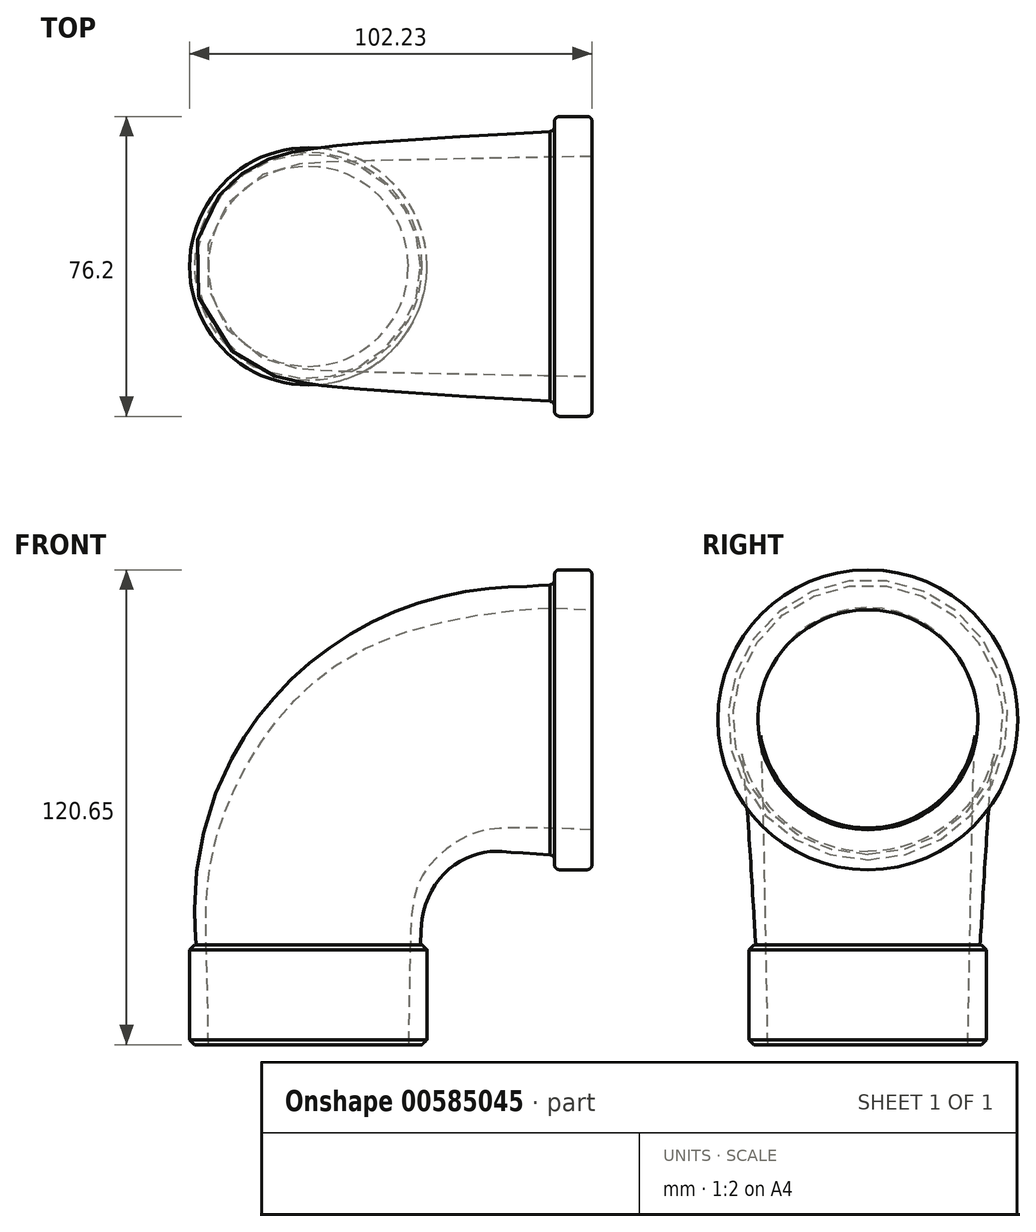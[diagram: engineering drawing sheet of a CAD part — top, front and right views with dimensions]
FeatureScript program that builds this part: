
annotation { "Feature Type Name" : "Feature", "Feature Type Description" : "" }
export const myFeature = defineFeature(function(context is Context, id is Id, definition is map)
    precondition{}
    {
        {
            var Q0;
            Q0=qCreatedBy(makeId("Top.planeOp"),FACE);
            var sketch = newSketch(context, id + "F0", { "sketchPlane" : qUnion([Q0])});
            skCircle(sketch, "E0", {"center": v(0, 0) * mm, "radius": 26.99 * mm});
            skCircle(sketch, "E1", {"center": v(0, 0) * mm, "radius": 25.4 * mm, "construction": true});
            skSolve(sketch);
        }
        {
            var Q0;
            Q0=qCreatedBy(makeId("Front.planeOp"),FACE);
            var sketch = newSketch(context, id + "F1", { "sketchPlane" : qUnion([Q0])});
            skLineSegment(sketch, "E2", {"start": v(0, 0) * mm, "end": v(0, 82.55) * mm, "construction": true});
            skLineSegment(sketch, "E3", {"start": v(0, 82.55) * mm, "end": v(72.07, 82.55) * mm, "construction": true});
            skArc(sketch, "E4", {"start": v(50.8, 82.55) * mm, "mid": v(14.88, 67.67) * mm, "end": v(0, 31.75) * mm});
            skLineSegment(sketch, "E5", {"start": v(0, 31.75) * mm, "end": v(0, 0) * mm});
            skLineSegment(sketch, "E6", {"start": v(72.07, 82.55) * mm, "end": v(50.8, 82.55) * mm});
            skSolve(sketch);
        }
        {
            var Q0;
            Q0=qCreatedBy(makeId("Right.planeOp"),FACE);
            var Q1;
            Q1=sQuery(id+"F1.wireOp",VERTEX,"E3.end");
            cPlane(context, id + "F2", {"entities" : qUnion([Q0, Q1]), "cplaneType" : CPlaneType.PLANE_POINT, "offset" : 25.4 * mm, "width" : 152.4 * mm, "height" : 152.4 * mm});
        }
        {
            var Q0;
            Q0=qCreatedBy(id+"F2.planeOp",FACE);
            var sketch = newSketch(context, id + "F3", { "sketchPlane" : qUnion([Q0])});
            skCircle(sketch, "E7", {"center": v(0, 82.55) * mm, "radius": 34.93 * mm});
            skCircle(sketch, "E8", {"center": v(0, 82.55) * mm, "radius": 27.94 * mm, "construction": true});
            skSolve(sketch);
        }
        {
            var Q0;
            Q0=makeQuery(id+"F0.imprint","IMPRINT",FACE,{"disambiguationData":[TD([[makeQuery(id+"F0.imprint","IMPRINT",EDGE,{"derivedFrom":sQuery(id+"F0.wireOp",EDGE,"E0")}),1.0]])]});
            var Q1;
            Q1=makeQuery(id+"F3.imprint","IMPRINT",FACE,{"disambiguationData":[TD([[makeQuery(id+"F3.imprint","IMPRINT",EDGE,{"derivedFrom":sQuery(id+"F3.wireOp",EDGE,"E7")}),1.0]])]});
            var Q2;
            Q2=sQuery(id+"F1.wireOp",EDGE,"E5");
            var Q3;
            Q3=sQuery(id+"F1.wireOp",EDGE,"E4");
            var Q4;
            Q4=sQuery(id+"F1.wireOp",EDGE,"E6");
            loft(context, id + "F4", {"sheetProfilesArray" : [{ "sheetProfileEntities" : qUnion([Q0]) }, { "sheetProfileEntities" : qUnion([Q1]) }], "addSections" : true, "spine" : qUnion([Q2, Q3, Q4]), "sectionCount" : 20});
        }
        {
            var Q0;
            Q0=makeQuery(id+"F0.imprint","IMPRINT",FACE,{"disambiguationData":[TD([[makeQuery(id+"F0.imprint","IMPRINT",EDGE,{"derivedFrom":sQuery(id+"F0.wireOp",EDGE,"E0")}),1.0]])]});
            var sketch = newSketch(context, id + "F5", { "sketchPlane" : qUnion([Q0])});
            skCircle(sketch, "E9", {"center": v(0, 0) * mm, "radius": 25.4 * mm});
            skSolve(sketch);
        }
        {
            var Q0;
            Q0=makeQuery(id+"F3.imprint","IMPRINT",FACE,{"disambiguationData":[TD([[makeQuery(id+"F3.imprint","IMPRINT",EDGE,{"derivedFrom":sQuery(id+"F3.wireOp",EDGE,"E7")}),1.0]])]});
            var sketch = newSketch(context, id + "F6", { "sketchPlane" : qUnion([Q0])});
            skCircle(sketch, "E10", {"center": v(0, 82.55) * mm, "radius": 27.94 * mm});
            skSolve(sketch);
        }
        {
            var Q0;
            Q0=makeQuery(id+"F6.imprint","IMPRINT",FACE,{"disambiguationData":[TD([[makeQuery(id+"F6.imprint","IMPRINT",EDGE,{"derivedFrom":sQuery(id+"F6.wireOp",EDGE,"E10")}),1.0]])]});
            var Q1;
            Q1=makeQuery(id+"F5.imprint","IMPRINT",FACE,{"disambiguationData":[TD([[makeQuery(id+"F5.imprint","IMPRINT",EDGE,{"derivedFrom":sQuery(id+"F5.wireOp",EDGE,"E9")}),1.0]])]});
            var Q2;
            Q2=sQuery(id+"F1.wireOp",EDGE,"E5");
            var Q3;
            Q3=sQuery(id+"F1.wireOp",EDGE,"E4");
            var Q4;
            Q4=sQuery(id+"F1.wireOp",EDGE,"E6");
            loft(context, id + "F7", {"operationType" : NewBodyOperationType.REMOVE, "sheetProfilesArray" : [{ "sheetProfileEntities" : qUnion([Q0]) }, { "sheetProfileEntities" : qUnion([Q1]) }], "addSections" : true, "spine" : qUnion([Q2, Q3, Q4]), "sectionCount" : 5});
        }
        {
            var Q0;
            Q0=makeQuery(id+"F3.imprint","IMPRINT",FACE,{"disambiguationData":[TD([[makeQuery(id+"F3.imprint","IMPRINT",EDGE,{"derivedFrom":sQuery(id+"F3.wireOp",EDGE,"E7")}),1.0]])]});
            var sketch = newSketch(context, id + "F8", { "sketchPlane" : qUnion([Q0])});
            skCircle(sketch, "E11", {"center": v(0, 82.55) * mm, "radius": 38.1 * mm});
            skCircle(sketch, "E12", {"center": v(0, 82.55) * mm, "radius": 31.75 * mm});
            skSolve(sketch);
        }
        {
            var Q0;
            Q0 = qSketchRegion(id + "F8", true);
            extrude(context, id + "F9", {"entities" : qUnion([Q0]), "operationType" : NewBodyOperationType.ADD, "oppositeDirection" : true, "depth" : 9.52 * mm, "offsetDistance" : 25.4 * mm});
        }
        {
            var Q0;
            Q0=makeQuery(id+"F9.boolean.opBoolean","INTERSECT",EDGE,{"derivedFrom":[makeQuery(id+"F4.opLoft","SWEPT_FACE",FACE,{"disambiguationData":[OSD([sQuery(id+"F0.wireOp",EDGE,"E0"),sQuery(id+"F3.wireOp",EDGE,"E7")])]}),makeQuery(id+"F9.opExtrude","CAP_FACE",FACE,{"disambiguationData":[OSD([sQuery(id+"F8.wireOp",EDGE,"E11"),sQuery(id+"F8.wireOp",EDGE,"E12")])],"isStart":false})]});
            var Q1;
            Q1=makeQuery(id+"F9.opExtrude","CAP_EDGE",EDGE,{"disambiguationData":[OSD([sQuery(id+"F8.wireOp",EDGE,"E11")])],"isStart":true});
            var Q2;
            Q2=makeQuery(id+"F9.opExtrude","CAP_EDGE",EDGE,{"disambiguationData":[OSD([sQuery(id+"F8.wireOp",EDGE,"E11")])],"isStart":false});
            fillet(context, id + "F10", {"entities" : qUnion([Q0, Q1, Q2]), "tangentPropagation" : true, "radius" : 1.27 * mm, "defaultsChanged" : true, "vertexSettings" : [], "allowEdgeOverflow" : false});
        }
        {
            var Q0;
            Q0=makeQuery(id+"F0.imprint","IMPRINT",FACE,{"disambiguationData":[TD([[makeQuery(id+"F0.imprint","IMPRINT",EDGE,{"derivedFrom":sQuery(id+"F0.wireOp",EDGE,"E0")}),1.0]])]});
            var sketch = newSketch(context, id + "F11", { "sketchPlane" : qUnion([Q0])});
            skCircle(sketch, "E13", {"center": v(0, 0) * mm, "radius": 30.16 * mm});
            skCircle(sketch, "E14", {"center": v(0, 0) * mm, "radius": 26.67 * mm});
            skSolve(sketch);
        }
        {
            var Q0;
            Q0 = qSketchRegion(id + "F11", true);
            extrude(context, id + "F12", {"entities" : qUnion([Q0]), "operationType" : NewBodyOperationType.ADD, "depth" : 25.4 * mm, "offsetDistance" : 25.4 * mm});
        }
        {
            var Q0;
            Q0=makeQuery(id+"F12.opExtrude","CAP_EDGE",EDGE,{"disambiguationData":[OSD([sQuery(id+"F11.wireOp",EDGE,"E13")])],"isStart":true});
            var Q1;
            Q1=makeQuery(id+"F12.opExtrude","CAP_EDGE",EDGE,{"disambiguationData":[OSD([sQuery(id+"F11.wireOp",EDGE,"E13")])],"isStart":false});
            chamfer(context, id + "F13", {"entities" : qUnion([Q0, Q1]), "width" : 1.27 * mm, "tangentPropagation" : true});
        }
    });
